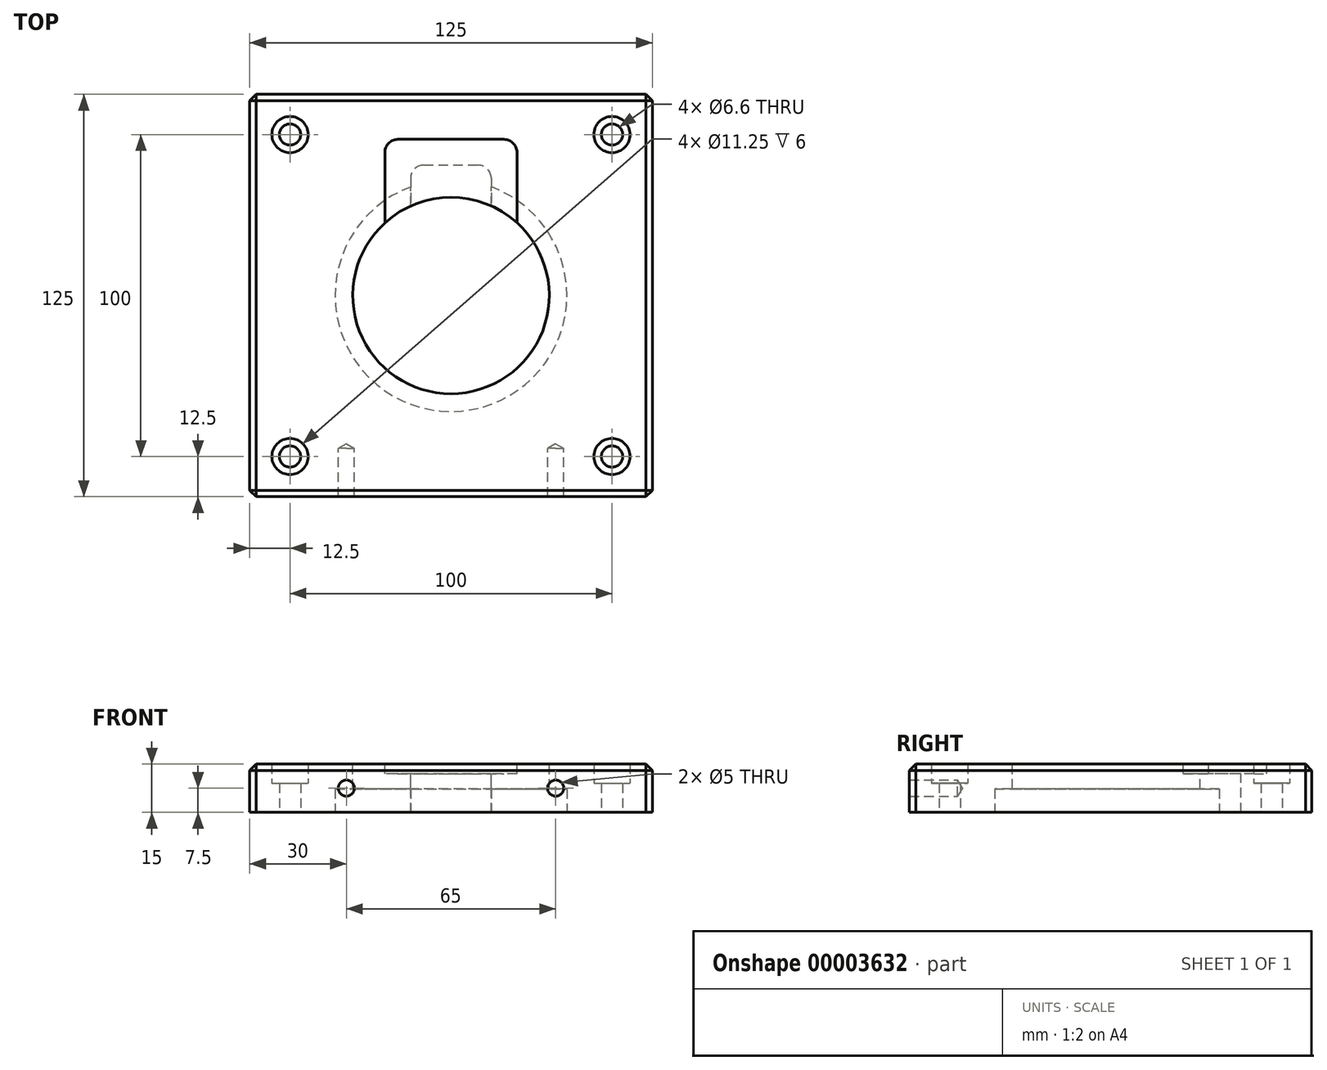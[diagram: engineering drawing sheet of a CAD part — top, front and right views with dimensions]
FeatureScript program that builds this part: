
annotation { "Feature Type Name" : "Feature", "Feature Type Description" : "" }
export const myFeature = defineFeature(function(context is Context, id is Id, definition is map)
    precondition{}
    {
        {
            var Q0;
            Q0=qCreatedBy(makeId("Top.planeOp"),FACE);
            var sketch = newSketch(context, id + "F0", { "sketchPlane" : qUnion([Q0])});
            skLineSegment(sketch, "E0.bottom", {"start": v(0, 0) * mm, "end": v(-125, 0) * mm});
            skLineSegment(sketch, "E0.top", {"start": v(0, 125) * mm, "end": v(-125, 125) * mm});
            skLineSegment(sketch, "E0.left", {"start": v(0, 0) * mm, "end": v(0, 125) * mm});
            skLineSegment(sketch, "E0.right", {"start": v(-125, 0) * mm, "end": v(-125, 125) * mm});
            skSolve(sketch);
        }
        {
            var Q0;
            Q0=makeQuery(id+"F0.imprint","IMPRINT",FACE,{"disambiguationData":[TD([[makeQuery(id+"F0.imprint","IMPRINT",EDGE,{"derivedFrom":sQuery(id+"F0.wireOp",EDGE,"E0.bottom")}),-1.0]])]});
            extrude(context, id + "F1", {"entities" : qUnion([Q0]), "depth" : 15 * mm});
        }
        {
            var Q0;
            Q0=makeQuery(id+"F1.opExtrude","CAP_EDGE",EDGE,{"disambiguationData":[OSD([sQuery(id+"F0.wireOp",EDGE,"E0.bottom")])],"isStart":false});
            var Q1;
            Q1=makeQuery(id+"F1.opExtrude","CAP_EDGE",EDGE,{"disambiguationData":[OSD([sQuery(id+"F0.wireOp",EDGE,"E0.left")])],"isStart":false});
            var Q2;
            Q2=makeQuery(id+"F1.opExtrude","CAP_EDGE",EDGE,{"disambiguationData":[OSD([sQuery(id+"F0.wireOp",EDGE,"E0.top")])],"isStart":false});
            var Q3;
            Q3=makeQuery(id+"F1.opExtrude","CAP_EDGE",EDGE,{"disambiguationData":[OSD([sQuery(id+"F0.wireOp",EDGE,"E0.right")])],"isStart":false});
            var Q4;
            Q4=makeQuery(id+"F1.opExtrude","SWEPT_EDGE",EDGE,{"disambiguationData":[OSD([sQuery(id+"F0.wireOp",EDGE,"E0.bottom"),sQuery(id+"F0.wireOp",EDGE,"E0.left")])]});
            var Q5;
            Q5=makeQuery(id+"F1.opExtrude","SWEPT_EDGE",EDGE,{"disambiguationData":[OSD([sQuery(id+"F0.wireOp",EDGE,"E0.top"),sQuery(id+"F0.wireOp",EDGE,"E0.left")])]});
            var Q6;
            Q6=makeQuery(id+"F1.opExtrude","SWEPT_EDGE",EDGE,{"disambiguationData":[OSD([sQuery(id+"F0.wireOp",EDGE,"E0.top"),sQuery(id+"F0.wireOp",EDGE,"E0.right")])]});
            var Q7;
            Q7=makeQuery(id+"F1.opExtrude","SWEPT_EDGE",EDGE,{"disambiguationData":[OSD([sQuery(id+"F0.wireOp",EDGE,"E0.bottom"),sQuery(id+"F0.wireOp",EDGE,"E0.right")])]});
            chamfer(context, id + "F2", {"entities" : qUnion([Q0, Q1, Q2, Q3, Q4, Q5, Q6, Q7]), "width" : 2 * mm, "tangentPropagation" : true});
        }
        {
            var Q0;
            Q0=makeQuery(id+"F1.opExtrude","CAP_FACE",FACE,{"disambiguationData":[OSD([sQuery(id+"F0.wireOp",EDGE,"E0.bottom"),sQuery(id+"F0.wireOp",EDGE,"E0.top"),sQuery(id+"F0.wireOp",EDGE,"E0.left"),sQuery(id+"F0.wireOp",EDGE,"E0.right")])],"isStart":false});
            var sketch = newSketch(context, id + "F3", { "sketchPlane" : qUnion([Q0])});
            skPoint(sketch, "E1", {"position": v(-112.5, 112.5) * mm});
            skPoint(sketch, "E2", {"position": v(-12.5, 112.5) * mm});
            skPoint(sketch, "E3", {"position": v(-12.5, 12.5) * mm});
            skPoint(sketch, "E4", {"position": v(-112.5, 12.5) * mm});
            skSolve(sketch);
        }
        {
            var Q0;
            Q0=sQuery(id+"F3.wireOp",VERTEX,"E1");
            var Q1;
            Q1=sQuery(id+"F3.wireOp",VERTEX,"E2");
            var Q2;
            Q2=sQuery(id+"F3.wireOp",VERTEX,"E3");
            var Q3;
            Q3=sQuery(id+"F3.wireOp",VERTEX,"E4");
            var Q4;
            Q4=makeQuery(id+"F1.opExtrude","SWEPT_BODY",BODY,{"disambiguationData":[OSD([sQuery(id+"F0.wireOp",EDGE,"E0.bottom"),sQuery(id+"F0.wireOp",EDGE,"E0.top"),sQuery(id+"F0.wireOp",EDGE,"E0.left"),sQuery(id+"F0.wireOp",EDGE,"E0.right")])]});
            hole(context, id + "F4", {"style" : HoleStyle.C_BORE, "endStyle" : HoleEndStyle.THROUGH, "standardTappedOrClearance" : lookupTablePath({ "standard" : "ISO", "fit" : "Normal", "size" : "M6", "type" : "Clearance" }), "standardBlindInLast" : lookupTablePath({ "fit" : "Standard", "standard" : "ISO", "size" : "M6", "type" : "Clearance" }), "holeDiameter" : 6.6 * mm, "cBoreDiameter" : 11.25 * mm, "cBoreDepth" : 6 * mm, "tappedDepth" : 7 * mm, "tapClearance" : 3, "locations" : qUnion([Q0, Q1, Q2, Q3]), "scope" : qUnion([Q4]), "startStyle" : HoleStartStyle.SKETCH});
        }
        {
            var Q0;
            Q0=makeQuery(id+"F1.opExtrude","CAP_FACE",FACE,{"disambiguationData":[OSD([sQuery(id+"F0.wireOp",EDGE,"E0.bottom"),sQuery(id+"F0.wireOp",EDGE,"E0.top"),sQuery(id+"F0.wireOp",EDGE,"E0.left"),sQuery(id+"F0.wireOp",EDGE,"E0.right")])],"isStart":false});
            var sketch = newSketch(context, id + "F5", { "sketchPlane" : qUnion([Q0])});
            skCircle(sketch, "E5", {"center": v(-62.5, 62.5) * mm, "radius": 30.5 * mm});
            skCircle(sketch, "E6", {"center": v(-62.5, 62.5) * mm, "radius": 36 * mm});
            skSolve(sketch);
        }
        {
            var Q0;
            Q0=makeQuery(id+"F5.imprint","IMPRINT",FACE,{"disambiguationData":[TD([[makeQuery(id+"F5.imprint","IMPRINT",EDGE,{"derivedFrom":sQuery(id+"F5.wireOp",EDGE,"E5")}),1.0]])]});
            extrude(context, id + "F6", {"entities" : qUnion([Q0]), "operationType" : NewBodyOperationType.REMOVE, "endBound" : BoundingType.THROUGH_ALL, "oppositeDirection" : true, "depth" : 25 * mm});
        }
        {
            var Q0;
            Q0=makeQuery(id+"F1.opExtrude","CAP_FACE",FACE,{"disambiguationData":[OSD([sQuery(id+"F0.wireOp",EDGE,"E0.bottom"),sQuery(id+"F0.wireOp",EDGE,"E0.top"),sQuery(id+"F0.wireOp",EDGE,"E0.left"),sQuery(id+"F0.wireOp",EDGE,"E0.right")])],"isStart":true});
            var sketch = newSketch(context, id + "F7", { "sketchPlane" : qUnion([Q0])});
            skCircle(sketch, "E7", {"center": v(-62.5, -62.5) * mm, "radius": 36 * mm});
            skSolve(sketch);
        }
        {
            var Q0;
            Q0=makeQuery(id+"F7.imprint","IMPRINT",FACE,{"disambiguationData":[TD([[makeQuery(id+"F7.imprint","IMPRINT",EDGE,{"derivedFrom":sQuery(id+"F7.wireOp",EDGE,"E7")}),1.0]])]});
            extrude(context, id + "F8", {"entities" : qUnion([Q0]), "operationType" : NewBodyOperationType.REMOVE, "oppositeDirection" : true, "depth" : 7.25 * mm});
        }
        {
            var Q0;
            Q0=makeQuery(id+"F1.opExtrude","CAP_FACE",FACE,{"disambiguationData":[OSD([sQuery(id+"F0.wireOp",EDGE,"E0.bottom"),sQuery(id+"F0.wireOp",EDGE,"E0.top"),sQuery(id+"F0.wireOp",EDGE,"E0.left"),sQuery(id+"F0.wireOp",EDGE,"E0.right")])],"isStart":false});
            var sketch = newSketch(context, id + "F9", { "sketchPlane" : qUnion([Q0])});
            skLineSegment(sketch, "E8", {"start": v(-71.02, 103) * mm, "end": v(-54.02, 103) * mm});
            skLineSegment(sketch, "E9", {"start": v(-75.02, 99) * mm, "end": v(-75.02, 90.31) * mm});
            skLineSegment(sketch, "E10", {"start": v(-50.02, 99) * mm, "end": v(-50.02, 90.33) * mm});
            skPoint(sketch, "E11.visualSharp", {"position": v(-75.02, 103) * mm});
            skArc(sketch, "E11.filletArc", {"start": v(-71.02, 103) * mm, "mid": v(-73.85, 101.83) * mm, "end": v(-75.02, 99) * mm});
            skPoint(sketch, "E12.visualSharp", {"position": v(-50.02, 103) * mm});
            skArc(sketch, "E12.filletArc", {"start": v(-50.02, 99) * mm, "mid": v(-51.19, 101.83) * mm, "end": v(-54.02, 103) * mm});
            skSolve(sketch);
        }
        {
            var Q0;
            Q0=makeQuery(id+"F9.imprint","IMPRINT",FACE,{"disambiguationData":[TD([[makeQuery(id+"F9.imprint","IMPRINT",EDGE,{"derivedFrom":sQuery(id+"F9.wireOp",EDGE,"E8")}),-1.0]])]});
            extrude(context, id + "F10", {"entities" : qUnion([Q0]), "operationType" : NewBodyOperationType.REMOVE, "endBound" : BoundingType.THROUGH_ALL, "oppositeDirection" : true, "depth" : 25 * mm});
        }
        {
            var Q0;
            Q0=makeQuery(id+"F9.imprint","IMPRINT",FACE,{"disambiguationData":[TD([[makeQuery(id+"F9.imprint","IMPRINT",EDGE,{"derivedFrom":sQuery(id+"F9.wireOp",EDGE,"E8")}),1.0]])]});
            var sketch = newSketch(context, id + "F11", { "sketchPlane" : qUnion([Q0])});
            skLineSegment(sketch, "E13", {"start": v(-79.02, 111) * mm, "end": v(-46.02, 111) * mm});
            skLineSegment(sketch, "E14", {"start": v(-42.02, 107) * mm, "end": v(-42.02, 77.92) * mm});
            skLineSegment(sketch, "E15", {"start": v(-83.02, 107) * mm, "end": v(-83.02, 83.45) * mm});
            skPoint(sketch, "E16.visualSharp", {"position": v(-83.02, 111) * mm});
            skArc(sketch, "E16.filletArc", {"start": v(-79.02, 111) * mm, "mid": v(-81.85, 109.83) * mm, "end": v(-83.02, 107) * mm});
            skPoint(sketch, "E17.visualSharp", {"position": v(-42.02, 111) * mm});
            skArc(sketch, "E17.filletArc", {"start": v(-42.02, 107) * mm, "mid": v(-43.19, 109.83) * mm, "end": v(-46.02, 111) * mm});
            skSolve(sketch);
        }
        {
            var Q0;
            Q0 = qSketchRegion(id + "F11", true);
            var Q1;
            Q1=makeQuery(id+"F11.imprint","IMPRINT",FACE,{"disambiguationData":[TD([[makeQuery(id+"F11.imprint","IMPRINT",EDGE,{"derivedFrom":sQuery(id+"F11.wireOp",EDGE,"E13")}),-1.0]])]});
            extrude(context, id + "F12", {"entities" : qUnion([Q0, Q1]), "operationType" : NewBodyOperationType.REMOVE, "oppositeDirection" : true, "depth" : 3 * mm});
        }
        {
            var Q0;
            Q0=makeQuery(id+"F1.opExtrude","SWEPT_FACE",FACE,{"disambiguationData":[OSD([sQuery(id+"F0.wireOp",EDGE,"E0.bottom")])]});
            var sketch = newSketch(context, id + "F13", { "sketchPlane" : qUnion([Q0])});
            skPoint(sketch, "E18", {"position": v(-95, 7.5) * mm});
            skPoint(sketch, "E19", {"position": v(-30, 7.5) * mm});
            skSolve(sketch);
        }
        {
            var Q0;
            Q0=sQuery(id+"F13.wireOp",VERTEX,"E18");
            var Q1;
            Q1=sQuery(id+"F13.wireOp",VERTEX,"E19");
            var Q2;
            Q2=makeQuery(id+"F1.opExtrude","SWEPT_BODY",BODY,{"disambiguationData":[OSD([sQuery(id+"F0.wireOp",EDGE,"E0.bottom"),sQuery(id+"F0.wireOp",EDGE,"E0.top"),sQuery(id+"F0.wireOp",EDGE,"E0.left"),sQuery(id+"F0.wireOp",EDGE,"E0.right")])]});
            hole(context, id + "F14", {"style" : HoleStyle.SIMPLE, "endStyle" : HoleEndStyle.BLIND, "standardTappedOrClearance" : lookupTablePath({ "standard" : "ISO", "engagement" : "75%", "pitch" : "1 mm", "size" : "M6", "type" : "Tapped" }), "standardBlindInLast" : lookupTablePath({ "standard" : "ISO", "engagement" : "75%", "pitch" : "1 mm", "size" : "M6", "type" : "Tapped" }), "holeDiameter" : 5 * mm, "showTappedDepth" : true, "holeDepth" : 15 * mm, "tappedDepth" : 12 * mm, "tapClearance" : 3, "locations" : qUnion([Q0, Q1]), "scope" : qUnion([Q2]), "majorDiameter" : 6 * mm, "startStyle" : HoleStartStyle.SKETCH});
        }
        {
            var Q0;
            Q0=makeQuery(id+"F9.imprint","IMPRINT",FACE,{"disambiguationData":[TD([[makeQuery(id+"F9.imprint","IMPRINT",EDGE,{"derivedFrom":sQuery(id+"F9.wireOp",EDGE,"E8")}),1.0]])]});
            var sketch = newSketch(context, id + "F15", { "sketchPlane" : qUnion([Q0])});
            skLineSegment(sketch, "E20.0", {"start": v(-83.02, 107) * mm, "end": v(-83.02, 85.07) * mm});
            skLineSegment(sketch, "E20.1", {"start": v(-42.02, 107) * mm, "end": v(-42.02, 85.1) * mm});
            skArc(sketch, "E20.2", {"start": v(-42.02, 107) * mm, "mid": v(-43.19, 109.83) * mm, "end": v(-46.02, 111) * mm});
            skLineSegment(sketch, "E20.3", {"start": v(-79.02, 111) * mm, "end": v(-46.02, 111) * mm});
            skArc(sketch, "E20.4", {"start": v(-79.02, 111) * mm, "mid": v(-81.85, 109.83) * mm, "end": v(-83.02, 107) * mm});
            skArc(sketch, "E21", {"start": v(-42.02, 85.1) * mm, "mid": v(-62.52, 93) * mm, "end": v(-83.02, 85.07) * mm});
            skSolve(sketch);
        }
        {
            var Q0;
            Q0 = qSketchRegion(id + "F15", true);
            extrude(context, id + "F16", {"entities" : qUnion([Q0]), "oppositeDirection" : true, "depth" : 3 * mm});
        }
    });
